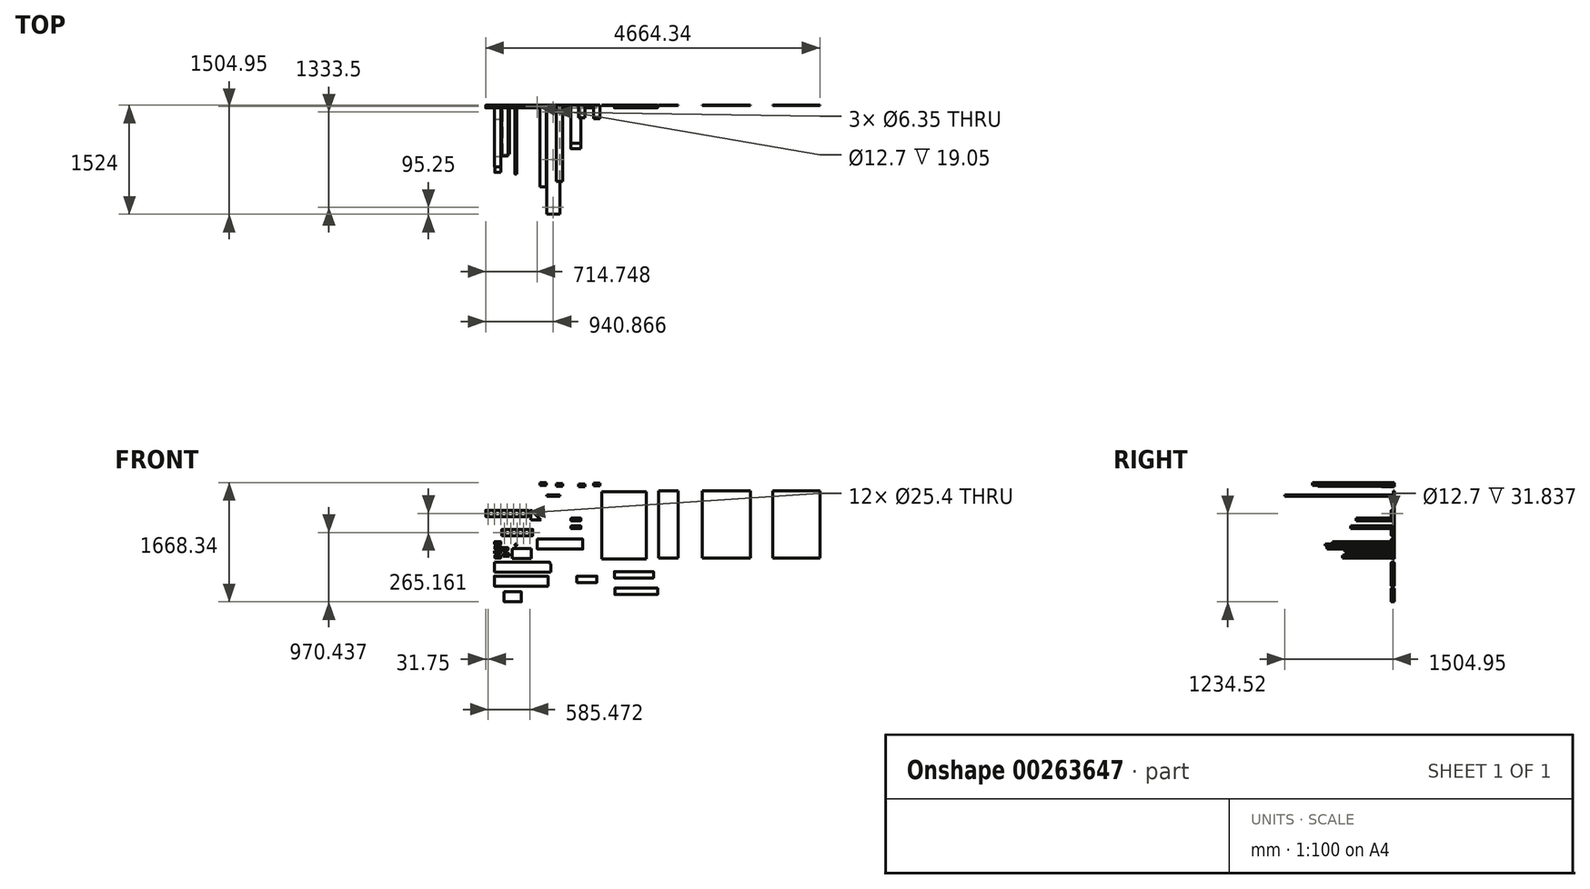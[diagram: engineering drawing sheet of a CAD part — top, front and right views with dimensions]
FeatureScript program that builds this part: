
annotation { "Feature Type Name" : "Feature", "Feature Type Description" : "" }
export const myFeature = defineFeature(function(context is Context, id is Id, definition is map)
    precondition{}
    {
        {
            var Q0;
            Q0=qCreatedBy(makeId("Front.planeOp"),FACE);
            var sketch = newSketch(context, id + "F0", { "sketchPlane" : qUnion([Q0])});
            skLineSegment(sketch, "E0.bottom", {"start": v(-85.66, 61.4) * mm, "end": v(3.24, 61.4) * mm});
            skLineSegment(sketch, "E0.top", {"start": v(-85.66, 23.3) * mm, "end": v(3.24, 23.3) * mm});
            skLineSegment(sketch, "E0.left", {"start": v(-85.66, 61.4) * mm, "end": v(-85.66, 23.3) * mm});
            skLineSegment(sketch, "E0.right", {"start": v(3.24, 61.4) * mm, "end": v(3.24, 23.3) * mm});
            skLineSegment(sketch, "E1.bottom", {"start": v(-85.72, -3.77) * mm, "end": v(3.18, -3.77) * mm});
            skLineSegment(sketch, "E1.top", {"start": v(-85.72, -41.87) * mm, "end": v(3.18, -41.87) * mm});
            skLineSegment(sketch, "E1.left", {"start": v(-85.72, -3.77) * mm, "end": v(-85.72, -41.87) * mm});
            skLineSegment(sketch, "E1.right", {"start": v(3.18, -3.77) * mm, "end": v(3.18, -41.87) * mm});
            skLineSegment(sketch, "E2.bottom", {"start": v(1.48, 88.2) * mm, "end": v(-87.42, 88.2) * mm});
            skLineSegment(sketch, "E2.top", {"start": v(1.48, 126.3) * mm, "end": v(-87.42, 126.3) * mm});
            skLineSegment(sketch, "E2.left", {"start": v(1.48, 88.2) * mm, "end": v(1.48, 126.3) * mm});
            skLineSegment(sketch, "E2.right", {"start": v(-87.42, 88.2) * mm, "end": v(-87.42, 126.3) * mm});
            skLineSegment(sketch, "E3.bottom", {"start": v(3.31, -67.16) * mm, "end": v(-85.59, -67.16) * mm});
            skLineSegment(sketch, "E3.top", {"start": v(3.31, -105.26) * mm, "end": v(-85.59, -105.26) * mm});
            skLineSegment(sketch, "E3.left", {"start": v(3.31, -67.16) * mm, "end": v(3.31, -105.26) * mm});
            skLineSegment(sketch, "E3.right", {"start": v(-85.59, -67.16) * mm, "end": v(-85.59, -105.26) * mm});
            skLineSegment(sketch, "E4.bottom", {"start": v(11.64, 44.1) * mm, "end": v(100.54, 44.1) * mm});
            skLineSegment(sketch, "E4.top", {"start": v(11.64, 6) * mm, "end": v(100.54, 6) * mm});
            skLineSegment(sketch, "E4.left", {"start": v(11.64, 44.1) * mm, "end": v(11.64, 6) * mm});
            skLineSegment(sketch, "E4.right", {"start": v(100.54, 44.1) * mm, "end": v(100.54, 6) * mm});
            skLineSegment(sketch, "E5.bottom", {"start": v(-86.6, -302.76) * mm, "end": v(700.8, -302.76) * mm});
            skLineSegment(sketch, "E5.top", {"start": v(-86.6, -163.06) * mm, "end": v(700.8, -163.06) * mm});
            skLineSegment(sketch, "E5.left", {"start": v(-86.6, -302.76) * mm, "end": v(-86.6, -163.06) * mm});
            skLineSegment(sketch, "E5.right", {"start": v(700.8, -302.76) * mm, "end": v(700.8, -163.06) * mm});
            skLineSegment(sketch, "E6.bottom", {"start": v(425.94, -111) * mm, "end": v(159.24, -111) * mm});
            skLineSegment(sketch, "E6.top", {"start": v(425.94, 28.7) * mm, "end": v(159.24, 28.7) * mm});
            skLineSegment(sketch, "E6.left", {"start": v(425.94, -111) * mm, "end": v(425.94, 28.7) * mm});
            skLineSegment(sketch, "E6.right", {"start": v(159.24, -111) * mm, "end": v(159.24, 28.7) * mm});
            skLineSegment(sketch, "E7.bottom", {"start": v(31.64, -41.5) * mm, "end": v(120.54, -41.5) * mm});
            skLineSegment(sketch, "E7.top", {"start": v(31.64, -79.6) * mm, "end": v(120.54, -79.6) * mm});
            skLineSegment(sketch, "E7.left", {"start": v(31.64, -41.5) * mm, "end": v(31.64, -79.6) * mm});
            skLineSegment(sketch, "E7.right", {"start": v(120.54, -41.5) * mm, "end": v(120.54, -79.6) * mm});
            skLineSegment(sketch, "E8.bottom", {"start": v(178.07, 132.2) * mm, "end": v(266.97, 132.2) * mm});
            skLineSegment(sketch, "E8.top", {"start": v(178.07, 94.1) * mm, "end": v(266.97, 94.1) * mm});
            skLineSegment(sketch, "E8.left", {"start": v(178.07, 132.2) * mm, "end": v(178.07, 94.1) * mm});
            skLineSegment(sketch, "E8.right", {"start": v(266.97, 132.2) * mm, "end": v(266.97, 94.1) * mm});
            skCircle(sketch, "E9", {"center": v(210, 76.86) * mm, "radius": 12.7 * mm});
            skLineSegment(sketch, "E10.bottom", {"start": v(13.97, 297.46) * mm, "end": v(445.77, 297.46) * mm});
            skLineSegment(sketch, "E10.top", {"start": v(13.97, 208.56) * mm, "end": v(445.77, 208.56) * mm});
            skLineSegment(sketch, "E10.left", {"start": v(13.97, 297.46) * mm, "end": v(13.97, 208.56) * mm});
            skLineSegment(sketch, "E10.right", {"start": v(445.77, 297.46) * mm, "end": v(445.77, 208.56) * mm});
            skLineSegment(sketch, "E11", {"start": v(13.97, 253) * mm, "end": v(52.07, 253) * mm});
            skLineSegment(sketch, "E12", {"start": v(52.07, 253) * mm, "end": v(140.97, 253) * mm});
            skLineSegment(sketch, "E13", {"start": v(140.97, 253) * mm, "end": v(229.87, 253) * mm});
            skLineSegment(sketch, "E14", {"start": v(229.87, 253) * mm, "end": v(318.77, 253) * mm});
            skCircle(sketch, "E15", {"center": v(52.07, 253) * mm, "radius": 12.7 * mm});
            skCircle(sketch, "E16", {"center": v(140.97, 253) * mm, "radius": 12.7 * mm});
            skCircle(sketch, "E17", {"center": v(229.87, 253) * mm, "radius": 12.7 * mm});
            skCircle(sketch, "E18", {"center": v(318.77, 253) * mm, "radius": 12.7 * mm});
            skLineSegment(sketch, "E19.bottom", {"start": v(-292.5, 427.6) * mm, "end": v(367.9, 427.6) * mm});
            skLineSegment(sketch, "E19.top", {"start": v(-292.5, 338.7) * mm, "end": v(367.9, 338.7) * mm});
            skLineSegment(sketch, "E19.left", {"start": v(-292.5, 427.6) * mm, "end": v(-292.5, 338.7) * mm});
            skLineSegment(sketch, "E19.right", {"start": v(367.9, 427.6) * mm, "end": v(367.9, 338.7) * mm});
            skLineSegment(sketch, "E20.bottom", {"start": v(-209.55, 562.62) * mm, "end": v(387.35, 562.62) * mm});
            skLineSegment(sketch, "E20.top", {"start": v(-209.55, 473.72) * mm, "end": v(387.35, 473.72) * mm});
            skLineSegment(sketch, "E20.left", {"start": v(-209.55, 562.62) * mm, "end": v(-209.55, 473.72) * mm});
            skLineSegment(sketch, "E20.right", {"start": v(387.35, 562.62) * mm, "end": v(387.35, 473.72) * mm});
            skLineSegment(sketch, "E21", {"start": v(-292.5, 383.15) * mm, "end": v(-254.4, 383.15) * mm});
            skLineSegment(sketch, "E22", {"start": v(-254.4, 383.15) * mm, "end": v(-152.8, 383.15) * mm});
            skLineSegment(sketch, "E23", {"start": v(-152.8, 383.15) * mm, "end": v(-51.2, 383.15) * mm});
            skLineSegment(sketch, "E24", {"start": v(-51.2, 383.15) * mm, "end": v(50.4, 383.15) * mm});
            skLineSegment(sketch, "E25", {"start": v(50.4, 383.15) * mm, "end": v(152, 383.15) * mm});
            skLineSegment(sketch, "E26", {"start": v(152, 383.15) * mm, "end": v(253.6, 383.15) * mm});
            skLineSegment(sketch, "E27", {"start": v(-209.55, 518.17) * mm, "end": v(-177.8, 518.17) * mm});
            skLineSegment(sketch, "E28", {"start": v(-177.8, 518.17) * mm, "end": v(-88.9, 518.17) * mm});
            skLineSegment(sketch, "E29", {"start": v(-88.9, 518.17) * mm, "end": v(0, 518.17) * mm});
            skLineSegment(sketch, "E30", {"start": v(0, 518.17) * mm, "end": v(88.9, 518.17) * mm});
            skLineSegment(sketch, "E31", {"start": v(88.9, 518.17) * mm, "end": v(177.8, 518.17) * mm});
            skLineSegment(sketch, "E32", {"start": v(177.8, 518.17) * mm, "end": v(266.7, 518.17) * mm});
            skCircle(sketch, "E33", {"center": v(-177.8, 518.17) * mm, "radius": 12.7 * mm});
            skCircle(sketch, "E34", {"center": v(-88.9, 518.17) * mm, "radius": 12.7 * mm});
            skCircle(sketch, "E35", {"center": v(0, 518.17) * mm, "radius": 12.7 * mm});
            skCircle(sketch, "E36", {"center": v(88.9, 518.17) * mm, "radius": 12.7 * mm});
            skCircle(sketch, "E37", {"center": v(177.8, 518.17) * mm, "radius": 12.7 * mm});
            skCircle(sketch, "E38", {"center": v(266.7, 518.17) * mm, "radius": 12.7 * mm});
            skCircle(sketch, "E39", {"center": v(-254.4, 383.15) * mm, "radius": 12.7 * mm});
            skCircle(sketch, "E40", {"center": v(-152.8, 383.15) * mm, "radius": 12.7 * mm});
            skCircle(sketch, "E41", {"center": v(-51.2, 383.15) * mm, "radius": 12.7 * mm});
            skCircle(sketch, "E42", {"center": v(50.4, 383.15) * mm, "radius": 12.7 * mm});
            skCircle(sketch, "E43", {"center": v(152, 383.15) * mm, "radius": 12.7 * mm});
            skCircle(sketch, "E44", {"center": v(253.6, 383.15) * mm, "radius": 12.7 * mm});
            skLineSegment(sketch, "E45.bottom", {"start": v(700.8, -163.06) * mm, "end": v(688.1, -163.06) * mm});
            skLineSegment(sketch, "E45.top", {"start": v(700.8, -188.46) * mm, "end": v(688.1, -188.46) * mm});
            skLineSegment(sketch, "E45.left", {"start": v(700.8, -163.06) * mm, "end": v(700.8, -188.46) * mm});
            skLineSegment(sketch, "E45.right", {"start": v(688.1, -163.06) * mm, "end": v(688.1, -188.46) * mm});
            skLineSegment(sketch, "E46.bottom", {"start": v(-89.61, -357.84) * mm, "end": v(659.69, -357.84) * mm});
            skLineSegment(sketch, "E46.top", {"start": v(-89.61, -497.54) * mm, "end": v(659.69, -497.54) * mm});
            skLineSegment(sketch, "E46.left", {"start": v(-89.61, -357.84) * mm, "end": v(-89.61, -497.54) * mm});
            skLineSegment(sketch, "E46.right", {"start": v(659.69, -357.84) * mm, "end": v(659.69, -497.54) * mm});
            skLineSegment(sketch, "E47.bottom", {"start": v(1407.38, 824.95) * mm, "end": v(2029.68, 824.95) * mm});
            skLineSegment(sketch, "E47.top", {"start": v(1407.38, -114.85) * mm, "end": v(2029.68, -114.85) * mm});
            skLineSegment(sketch, "E47.left", {"start": v(1407.38, 824.95) * mm, "end": v(1407.38, -114.85) * mm});
            skLineSegment(sketch, "E47.right", {"start": v(2029.68, 824.95) * mm, "end": v(2029.68, -114.85) * mm});
            skLineSegment(sketch, "E48.bottom", {"start": v(2204.45, 833.86) * mm, "end": v(2477.5, 833.86) * mm});
            skLineSegment(sketch, "E48.top", {"start": v(2204.45, -105.94) * mm, "end": v(2477.5, -105.94) * mm});
            skLineSegment(sketch, "E48.left", {"start": v(2204.45, 833.86) * mm, "end": v(2204.45, -105.94) * mm});
            skLineSegment(sketch, "E48.right", {"start": v(2477.5, 833.86) * mm, "end": v(2477.5, -105.94) * mm});
            skLineSegment(sketch, "E49.bottom", {"start": v(2811.62, 833.86) * mm, "end": v(3484.72, 833.86) * mm});
            skLineSegment(sketch, "E49.top", {"start": v(2811.62, -105.94) * mm, "end": v(3484.72, -105.94) * mm});
            skLineSegment(sketch, "E49.left", {"start": v(2811.62, 833.86) * mm, "end": v(2811.62, -105.94) * mm});
            skLineSegment(sketch, "E49.right", {"start": v(3484.72, 833.86) * mm, "end": v(3484.72, -105.94) * mm});
            skLineSegment(sketch, "E50", {"start": v(266.7, 518.17) * mm, "end": v(355.6, 518.17) * mm});
            skCircle(sketch, "E51", {"center": v(355.6, 518.17) * mm, "radius": 12.7 * mm});
            skLineSegment(sketch, "E52", {"start": v(318.77, 253) * mm, "end": v(407.67, 253) * mm});
            skCircle(sketch, "E53", {"center": v(407.67, 253) * mm, "radius": 12.7 * mm});
            skLineSegment(sketch, "E54.bottom", {"start": v(416.3, 567.9) * mm, "end": v(556, 567.9) * mm});
            skLineSegment(sketch, "E54.top", {"start": v(416.3, 428.2) * mm, "end": v(556, 428.2) * mm});
            skLineSegment(sketch, "E54.left", {"start": v(416.3, 567.9) * mm, "end": v(416.3, 428.2) * mm});
            skLineSegment(sketch, "E54.right", {"start": v(556, 567.9) * mm, "end": v(556, 428.2) * mm});
            skLineSegment(sketch, "E55", {"start": v(416.3, 567.9) * mm, "end": v(556, 428.2) * mm});
            skLineSegment(sketch, "E56.bottom", {"start": v(980.9, 453.14) * mm, "end": v(1120.6, 453.14) * mm});
            skLineSegment(sketch, "E56.top", {"start": v(980.9, 415.04) * mm, "end": v(1120.6, 415.04) * mm});
            skLineSegment(sketch, "E56.left", {"start": v(980.9, 453.14) * mm, "end": v(980.9, 415.04) * mm});
            skLineSegment(sketch, "E56.right", {"start": v(1120.6, 453.14) * mm, "end": v(1120.6, 415.04) * mm});
            skLineSegment(sketch, "E57.bottom", {"start": v(980.9, 343.92) * mm, "end": v(1120.6, 343.92) * mm});
            skLineSegment(sketch, "E57.top", {"start": v(980.9, 305.82) * mm, "end": v(1120.6, 305.82) * mm});
            skLineSegment(sketch, "E57.left", {"start": v(980.9, 343.92) * mm, "end": v(980.9, 305.82) * mm});
            skLineSegment(sketch, "E57.right", {"start": v(1120.6, 343.92) * mm, "end": v(1120.6, 305.82) * mm});
            skLineSegment(sketch, "E58.bottom", {"start": v(509.36, 160.8) * mm, "end": v(1144.36, 160.8) * mm});
            skLineSegment(sketch, "E58.top", {"start": v(509.36, 21.1) * mm, "end": v(1144.36, 21.1) * mm});
            skLineSegment(sketch, "E58.left", {"start": v(509.36, 160.8) * mm, "end": v(509.36, 21.1) * mm});
            skLineSegment(sketch, "E58.right", {"start": v(1144.36, 160.8) * mm, "end": v(1144.36, 21.1) * mm});
            skLineSegment(sketch, "E59.bottom", {"start": v(2132.43, -293.4) * mm, "end": v(1586.33, -293.4) * mm});
            skLineSegment(sketch, "E59.top", {"start": v(2132.43, -382.3) * mm, "end": v(1586.33, -382.3) * mm});
            skLineSegment(sketch, "E59.left", {"start": v(2132.43, -293.4) * mm, "end": v(2132.43, -382.3) * mm});
            skLineSegment(sketch, "E59.right", {"start": v(1586.33, -293.4) * mm, "end": v(1586.33, -382.3) * mm});
            skLineSegment(sketch, "E60.bottom", {"start": v(2190.62, -526.52) * mm, "end": v(1593.72, -526.52) * mm});
            skLineSegment(sketch, "E60.top", {"start": v(2190.62, -615.42) * mm, "end": v(1593.72, -615.42) * mm});
            skLineSegment(sketch, "E60.left", {"start": v(2190.62, -526.52) * mm, "end": v(2190.62, -615.42) * mm});
            skLineSegment(sketch, "E60.right", {"start": v(1593.72, -526.52) * mm, "end": v(1593.72, -615.42) * mm});
            skLineSegment(sketch, "E61.bottom", {"start": v(1062.38, -357.34) * mm, "end": v(1341.78, -357.34) * mm});
            skLineSegment(sketch, "E61.top", {"start": v(1062.38, -446.24) * mm, "end": v(1341.78, -446.24) * mm});
            skLineSegment(sketch, "E61.left", {"start": v(1062.38, -357.34) * mm, "end": v(1062.38, -446.24) * mm});
            skLineSegment(sketch, "E61.right", {"start": v(1341.78, -357.34) * mm, "end": v(1341.78, -446.24) * mm});
            skLineSegment(sketch, "E62.bottom", {"start": v(47.05, -577.73) * mm, "end": v(288.35, -577.73) * mm});
            skLineSegment(sketch, "E62.top", {"start": v(47.05, -717.43) * mm, "end": v(288.35, -717.43) * mm});
            skLineSegment(sketch, "E62.left", {"start": v(47.05, -577.73) * mm, "end": v(47.05, -717.43) * mm});
            skLineSegment(sketch, "E62.right", {"start": v(288.35, -577.73) * mm, "end": v(288.35, -717.43) * mm});
            skLineSegment(sketch, "E63.bottom", {"start": v(3794.39, 833.86) * mm, "end": v(4454.79, 833.86) * mm});
            skLineSegment(sketch, "E63.top", {"start": v(3794.39, -105.94) * mm, "end": v(4454.79, -105.94) * mm});
            skLineSegment(sketch, "E63.left", {"start": v(3794.39, 833.86) * mm, "end": v(3794.39, -105.94) * mm});
            skLineSegment(sketch, "E63.right", {"start": v(4454.79, 833.86) * mm, "end": v(4454.79, -105.94) * mm});
            skLineSegment(sketch, "E64.bottom", {"start": v(549.17, 950.91) * mm, "end": v(638.07, 950.91) * mm});
            skLineSegment(sketch, "E64.top", {"start": v(549.17, 912.81) * mm, "end": v(638.07, 912.81) * mm});
            skLineSegment(sketch, "E64.left", {"start": v(549.17, 950.91) * mm, "end": v(549.17, 912.81) * mm});
            skLineSegment(sketch, "E64.right", {"start": v(638.07, 950.91) * mm, "end": v(638.07, 912.81) * mm});
            skLineSegment(sketch, "E65.bottom", {"start": v(774.22, 935.7) * mm, "end": v(863.12, 935.7) * mm});
            skLineSegment(sketch, "E65.top", {"start": v(774.22, 897.6) * mm, "end": v(863.12, 897.6) * mm});
            skLineSegment(sketch, "E65.left", {"start": v(774.22, 935.7) * mm, "end": v(774.22, 897.6) * mm});
            skLineSegment(sketch, "E65.right", {"start": v(863.12, 935.7) * mm, "end": v(863.12, 897.6) * mm});
            skLineSegment(sketch, "E66.bottom", {"start": v(1087.47, 929.62) * mm, "end": v(1176.37, 929.62) * mm});
            skLineSegment(sketch, "E66.top", {"start": v(1087.47, 891.52) * mm, "end": v(1176.37, 891.52) * mm});
            skLineSegment(sketch, "E66.left", {"start": v(1087.47, 929.62) * mm, "end": v(1087.47, 891.52) * mm});
            skLineSegment(sketch, "E66.right", {"start": v(1176.37, 929.62) * mm, "end": v(1176.37, 891.52) * mm});
            skLineSegment(sketch, "E67.bottom", {"start": v(1293.65, 941.37) * mm, "end": v(1382.55, 941.37) * mm});
            skLineSegment(sketch, "E67.top", {"start": v(1293.65, 903.27) * mm, "end": v(1382.55, 903.27) * mm});
            skLineSegment(sketch, "E67.left", {"start": v(1293.65, 941.37) * mm, "end": v(1293.65, 903.27) * mm});
            skLineSegment(sketch, "E67.right", {"start": v(1382.55, 941.37) * mm, "end": v(1382.55, 903.27) * mm});
            skLineSegment(sketch, "E68.bottom", {"start": v(642.42, 775.35) * mm, "end": v(826.57, 775.35) * mm});
            skLineSegment(sketch, "E68.top", {"start": v(642.42, 756.3) * mm, "end": v(826.57, 756.3) * mm});
            skLineSegment(sketch, "E68.left", {"start": v(642.42, 775.35) * mm, "end": v(642.42, 756.3) * mm});
            skLineSegment(sketch, "E68.right", {"start": v(826.57, 775.35) * mm, "end": v(826.57, 756.3) * mm});
            skSolve(sketch);
        }
        {
            var Q0;
            Q0=makeQuery(id+"F0.imprint","IMPRINT",FACE,{"disambiguationData":[TD([[makeQuery(id+"F0.imprint","IMPRINT",EDGE,{"derivedFrom":sQuery(id+"F0.wireOp",EDGE,"E0.bottom")}),-1.0]])]});
            var Q1;
            {var subQ0=sQuery(id+"F0.wireOp",EDGE,"cPqlnZu6-hQf6-qhiV-5iE7-ykGDKPtnwq6q");var subQ4=makeQuery(id+"F0.imprint","IMPRINT",VERTEX,{"derivedFrom":subQ0});Q1=makeQuery(id+"F0.imprint","IMPRINT",FACE,{"disambiguationData":[TD([[makeQuery(id+"F0.imprint","IMPRINT",EDGE,{"disambiguationData":[TD([[subQ4,1.0]])],"derivedFrom":subQ0}),-1.0]])]});}
            extrude(context, id + "F1", {"entities" : qUnion([Q0, Q1]), "depth" : 939.8 * mm});
        }
        {
            var Q0;
            Q0=makeQuery(id+"F1.opExtrude","SWEPT_EDGE",EDGE,{"disambiguationData":[OSD([sQuery(id+"F0.wireOp",EDGE,"E0.bottom"),sQuery(id+"F0.wireOp",EDGE,"E0.left")])]});
            var Q1;
            Q1=makeQuery(id+"F1.opExtrude","SWEPT_EDGE",EDGE,{"disambiguationData":[OSD([sQuery(id+"F0.wireOp",EDGE,"E0.top"),sQuery(id+"F0.wireOp",EDGE,"E0.left")])]});
            var Q2;
            Q2=makeQuery(id+"F1.opExtrude","SWEPT_EDGE",EDGE,{"disambiguationData":[OSD([sQuery(id+"F0.wireOp",EDGE,"E0.bottom"),sQuery(id+"F0.wireOp",EDGE,"E0.right")])]});
            var Q3;
            Q3=makeQuery(id+"F1.opExtrude","SWEPT_EDGE",EDGE,{"disambiguationData":[OSD([sQuery(id+"F0.wireOp",EDGE,"E0.top"),sQuery(id+"F0.wireOp",EDGE,"E0.right")])]});
            fillet(context, id + "F2", {"entities" : qUnion([Q0, Q1, Q2, Q3]), "radius" : 5.08 * mm, "tangentPropagation" : true, "allowEdgeOverflow" : false});
        }
        {
            var Q0;
            Q0=makeQuery(id+"F0.imprint","IMPRINT",FACE,{"disambiguationData":[TD([[makeQuery(id+"F0.imprint","IMPRINT",EDGE,{"derivedFrom":sQuery(id+"F0.wireOp",EDGE,"E2.bottom")}),-1.0]])]});
            extrude(context, id + "F3", {"entities" : qUnion([Q0]), "depth" : 863.6 * mm});
        }
        {
            var Q0;
            Q0=makeQuery(id+"F0.imprint","IMPRINT",FACE,{"disambiguationData":[TD([[makeQuery(id+"F0.imprint","IMPRINT",EDGE,{"derivedFrom":sQuery(id+"F0.wireOp",EDGE,"E4.bottom")}),-1.0]])]});
            extrude(context, id + "F4", {"entities" : qUnion([Q0]), "depth" : 711.2 * mm});
        }
        {
            var Q0;
            Q0=makeQuery(id+"F0.imprint","IMPRINT",FACE,{"disambiguationData":[TD([[makeQuery(id+"F0.imprint","IMPRINT",EDGE,{"derivedFrom":sQuery(id+"F0.wireOp",EDGE,"E6.bottom")}),-1.0]])]});
            extrude(context, id + "F5", {"entities" : qUnion([Q0]), "depth" : 38.1 * mm});
        }
        {
            var Q0;
            Q0=makeQuery(id+"F0.imprint","IMPRINT",FACE,{"disambiguationData":[TD([[makeQuery(id+"F0.imprint","IMPRINT",EDGE,{"derivedFrom":sQuery(id+"F0.wireOp",EDGE,"E5.bottom")}),1.0]])]});
            extrude(context, id + "F6", {"entities" : qUnion([Q0]), "depth" : 38.1 * mm});
        }
        {
            var Q0;
            Q0=makeQuery(id+"F3.opExtrude","SWEPT_EDGE",EDGE,{"disambiguationData":[OSD([sQuery(id+"F0.wireOp",EDGE,"E2.top"),sQuery(id+"F0.wireOp",EDGE,"E2.left")])]});
            var Q1;
            Q1=makeQuery(id+"F3.opExtrude","SWEPT_EDGE",EDGE,{"disambiguationData":[OSD([sQuery(id+"F0.wireOp",EDGE,"E2.bottom"),sQuery(id+"F0.wireOp",EDGE,"E2.left")])]});
            var Q2;
            Q2=makeQuery(id+"F4.opExtrude","SWEPT_EDGE",EDGE,{"disambiguationData":[OSD([sQuery(id+"F0.wireOp",EDGE,"E4.bottom"),sQuery(id+"F0.wireOp",EDGE,"E4.right")])]});
            var Q3;
            Q3=makeQuery(id+"F4.opExtrude","SWEPT_EDGE",EDGE,{"disambiguationData":[OSD([sQuery(id+"F0.wireOp",EDGE,"E4.top"),sQuery(id+"F0.wireOp",EDGE,"E4.right")])]});
            var Q4;
            Q4=makeQuery(id+"F6.opExtrude","CAP_EDGE",EDGE,{"disambiguationData":[OSD([sQuery(id+"F0.wireOp",EDGE,"E5.top")])],"isStart":false});
            var Q5;
            Q5=makeQuery(id+"F6.opExtrude","CAP_EDGE",EDGE,{"disambiguationData":[OSD([sQuery(id+"F0.wireOp",EDGE,"E5.top")])],"isStart":true});
            var Q6;
            Q6=makeQuery(id+"F5.opExtrude","CAP_EDGE",EDGE,{"disambiguationData":[OSD([sQuery(id+"F0.wireOp",EDGE,"E6.top")])],"isStart":false});
            var Q7;
            Q7=makeQuery(id+"F5.opExtrude","CAP_EDGE",EDGE,{"disambiguationData":[OSD([sQuery(id+"F0.wireOp",EDGE,"E6.top")])],"isStart":true});
            var Q8;
            Q8=makeQuery(id+"F4.opExtrude","SWEPT_EDGE",EDGE,{"disambiguationData":[OSD([sQuery(id+"F0.wireOp",EDGE,"E4.top"),sQuery(id+"F0.wireOp",EDGE,"E4.left")])]});
            var Q9;
            Q9=makeQuery(id+"F4.opExtrude","SWEPT_EDGE",EDGE,{"disambiguationData":[OSD([sQuery(id+"F0.wireOp",EDGE,"E4.bottom"),sQuery(id+"F0.wireOp",EDGE,"E4.left")])]});
            var Q10;
            Q10=makeQuery(id+"F3.opExtrude","SWEPT_EDGE",EDGE,{"disambiguationData":[OSD([sQuery(id+"F0.wireOp",EDGE,"E2.bottom"),sQuery(id+"F0.wireOp",EDGE,"E2.right")])]});
            var Q11;
            Q11=makeQuery(id+"F3.opExtrude","SWEPT_EDGE",EDGE,{"disambiguationData":[OSD([sQuery(id+"F0.wireOp",EDGE,"E2.top"),sQuery(id+"F0.wireOp",EDGE,"E2.right")])]});
            var Q12;
            Q12=makeQuery(id+"F6.opExtrude","CAP_EDGE",EDGE,{"disambiguationData":[OSD([sQuery(id+"F0.wireOp",EDGE,"E5.bottom")])],"isStart":false});
            var Q13;
            Q13=makeQuery(id+"F6.opExtrude","CAP_EDGE",EDGE,{"disambiguationData":[OSD([sQuery(id+"F0.wireOp",EDGE,"E5.bottom")])],"isStart":true});
            var Q14;
            Q14=makeQuery(id+"F5.opExtrude","CAP_EDGE",EDGE,{"disambiguationData":[OSD([sQuery(id+"F0.wireOp",EDGE,"E6.bottom")])],"isStart":false});
            var Q15;
            Q15=makeQuery(id+"F5.opExtrude","CAP_EDGE",EDGE,{"disambiguationData":[OSD([sQuery(id+"F0.wireOp",EDGE,"E6.bottom")])],"isStart":true});
            fillet(context, id + "F7", {"entities" : qUnion([Q0, Q1, Q2, Q3, Q4, Q5, Q6, Q7, Q8, Q9, Q10, Q11, Q12, Q13, Q14, Q15]), "radius" : 5.08 * mm, "tangentPropagation" : true, "allowEdgeOverflow" : false});
        }
        {
            var Q0;
            Q0=makeQuery(id+"F0.imprint","IMPRINT",FACE,{"disambiguationData":[TD([[makeQuery(id+"F0.imprint","IMPRINT",EDGE,{"derivedFrom":sQuery(id+"F0.wireOp",EDGE,"E3.bottom")}),1.0]])]});
            extrude(context, id + "F8", {"entities" : qUnion([Q0]), "depth" : 723.9 * mm});
        }
        {
            var Q0;
            Q0=makeQuery(id+"F8.opExtrude","SWEPT_EDGE",EDGE,{"disambiguationData":[OSD([sQuery(id+"F0.wireOp",EDGE,"E3.bottom"),sQuery(id+"F0.wireOp",EDGE,"E3.left")])]});
            var Q1;
            Q1=makeQuery(id+"F8.opExtrude","SWEPT_EDGE",EDGE,{"disambiguationData":[OSD([sQuery(id+"F0.wireOp",EDGE,"E3.bottom"),sQuery(id+"F0.wireOp",EDGE,"E3.right")])]});
            var Q2;
            Q2=makeQuery(id+"F8.opExtrude","SWEPT_EDGE",EDGE,{"disambiguationData":[OSD([sQuery(id+"F0.wireOp",EDGE,"E3.top"),sQuery(id+"F0.wireOp",EDGE,"E3.left")])]});
            var Q3;
            Q3=makeQuery(id+"F8.opExtrude","SWEPT_EDGE",EDGE,{"disambiguationData":[OSD([sQuery(id+"F0.wireOp",EDGE,"E3.top"),sQuery(id+"F0.wireOp",EDGE,"E3.right")])]});
            fillet(context, id + "F9", {"entities" : qUnion([Q0, Q1, Q2, Q3]), "radius" : 5.08 * mm, "tangentPropagation" : true, "allowEdgeOverflow" : false});
        }
        {
            var Q0;
            Q0=makeQuery(id+"F0.imprint","IMPRINT",FACE,{"disambiguationData":[TD([[makeQuery(id+"F0.imprint","IMPRINT",EDGE,{"derivedFrom":sQuery(id+"F0.wireOp",EDGE,"E1.bottom")}),-1.0]])]});
            extrude(context, id + "F10", {"entities" : qUnion([Q0]), "depth" : 196.85 * mm});
        }
        {
            var Q0;
            Q0=makeQuery(id+"F0.imprint","IMPRINT",FACE,{"disambiguationData":[TD([[makeQuery(id+"F0.imprint","IMPRINT",EDGE,{"derivedFrom":sQuery(id+"F0.wireOp",EDGE,"E7.bottom")}),-1.0]])]});
            extrude(context, id + "F11", {"entities" : qUnion([Q0]), "depth" : 685.8 * mm});
        }
        {
            var Q0;
            Q0=makeQuery(id+"F0.imprint","IMPRINT",FACE,{"disambiguationData":[TD([[makeQuery(id+"F0.imprint","IMPRINT",EDGE,{"derivedFrom":sQuery(id+"F0.wireOp",EDGE,"E8.bottom")}),-1.0]])]});
            extrude(context, id + "F12", {"entities" : qUnion([Q0]), "depth" : 571.5 * mm});
        }
        {
            var Q0;
            Q0=makeQuery(id+"F0.imprint","IMPRINT",FACE,{"disambiguationData":[TD([[makeQuery(id+"F0.imprint","IMPRINT",EDGE,{"derivedFrom":sQuery(id+"F0.wireOp",EDGE,"E9")}),1.0]])]});
            extrude(context, id + "F13", {"entities" : qUnion([Q0]), "depth" : 965.2 * mm});
        }
        {
            var Q0;
            {var subQ12=sQuery(id+"F0.wireOp",EDGE,"E10.bottom");Q0=makeQuery(id+"F0.imprint","IMPRINT",FACE,{"disambiguationData":[TD([[makeQuery(id+"F0.imprint","IMPRINT",EDGE,{"derivedFrom":subQ12}),-1.0]])]});}
            extrude(context, id + "F14", {"entities" : qUnion([Q0]), "depth" : 38.1 * mm});
        }
        {
            var Q0;
            Q0=makeQuery(id+"F12.opExtrude","SWEPT_BODY",BODY,{"disambiguationData":[OSD([sQuery(id+"F0.wireOp",EDGE,"E8.bottom"),sQuery(id+"F0.wireOp",EDGE,"E8.top"),sQuery(id+"F0.wireOp",EDGE,"E8.left"),sQuery(id+"F0.wireOp",EDGE,"E8.right")])]});
            deleteBodies(context, id + "F15", {"entities" : qUnion([Q0])});
        }
        {
            var Q0;
            {var subQ15=sQuery(id+"F0.wireOp",EDGE,"E20.bottom");Q0=makeQuery(id+"F0.imprint","IMPRINT",FACE,{"disambiguationData":[TD([[makeQuery(id+"F0.imprint","IMPRINT",EDGE,{"derivedFrom":subQ15}),-1.0]])]});}
            extrude(context, id + "F16", {"entities" : qUnion([Q0]), "depth" : 38.1 * mm});
        }
        {
            var Q0;
            Q0=makeQuery(id+"F16.opExtrude","CAP_EDGE",EDGE,{"disambiguationData":[OSD([sQuery(id+"F0.wireOp",EDGE,"E20.bottom")])],"isStart":false});
            var Q1;
            Q1=makeQuery(id+"F16.opExtrude","CAP_EDGE",EDGE,{"disambiguationData":[OSD([sQuery(id+"F0.wireOp",EDGE,"E20.top")])],"isStart":false});
            var Q2;
            Q2=makeQuery(id+"F16.opExtrude","CAP_EDGE",EDGE,{"disambiguationData":[OSD([sQuery(id+"F0.wireOp",EDGE,"E20.top")])],"isStart":true});
            var Q3;
            Q3=makeQuery(id+"F14.opExtrude","CAP_EDGE",EDGE,{"disambiguationData":[OSD([sQuery(id+"F0.wireOp",EDGE,"E10.bottom")])],"isStart":false});
            var Q4;
            Q4=makeQuery(id+"F14.opExtrude","CAP_EDGE",EDGE,{"disambiguationData":[OSD([sQuery(id+"F0.wireOp",EDGE,"E10.top")])],"isStart":false});
            var Q5;
            Q5=makeQuery(id+"F14.opExtrude","CAP_EDGE",EDGE,{"disambiguationData":[OSD([sQuery(id+"F0.wireOp",EDGE,"E10.top")])],"isStart":true});
            var Q6;
            Q6=makeQuery(id+"F14.opExtrude","CAP_EDGE",EDGE,{"disambiguationData":[OSD([sQuery(id+"F0.wireOp",EDGE,"E10.bottom")])],"isStart":true});
            var Q7;
            Q7=makeQuery(id+"F16.opExtrude","CAP_EDGE",EDGE,{"disambiguationData":[OSD([sQuery(id+"F0.wireOp",EDGE,"E20.bottom")])],"isStart":true});
            fillet(context, id + "F17", {"entities" : qUnion([Q0, Q1, Q2, Q3, Q4, Q5, Q6, Q7]), "radius" : 5.08 * mm, "tangentPropagation" : true, "allowEdgeOverflow" : false});
        }
        {
            var Q0;
            Q0=makeQuery(id+"F0.imprint","IMPRINT",FACE,{"disambiguationData":[TD([[makeQuery(id+"F0.imprint","IMPRINT",EDGE,{"derivedFrom":sQuery(id+"F0.wireOp",EDGE,"E46.bottom")}),-1.0]])]});
            extrude(context, id + "F18", {"entities" : qUnion([Q0]), "depth" : 38.1 * mm});
        }
        {
            var Q0;
            Q0=makeQuery(id+"F18.opExtrude","CAP_EDGE",EDGE,{"disambiguationData":[OSD([sQuery(id+"F0.wireOp",EDGE,"E46.bottom")])],"isStart":false});
            var Q1;
            Q1=makeQuery(id+"F18.opExtrude","CAP_EDGE",EDGE,{"disambiguationData":[OSD([sQuery(id+"F0.wireOp",EDGE,"E46.top")])],"isStart":false});
            var Q2;
            Q2=makeQuery(id+"F18.opExtrude","CAP_EDGE",EDGE,{"disambiguationData":[OSD([sQuery(id+"F0.wireOp",EDGE,"E46.bottom")])],"isStart":true});
            var Q3;
            Q3=makeQuery(id+"F18.opExtrude","CAP_EDGE",EDGE,{"disambiguationData":[OSD([sQuery(id+"F0.wireOp",EDGE,"E46.top")])],"isStart":true});
            fillet(context, id + "F19", {"entities" : qUnion([Q0, Q1, Q2, Q3]), "radius" : 5.08 * mm, "tangentPropagation" : true, "allowEdgeOverflow" : false});
        }
        {
            var Q0;
            Q0=makeQuery(id+"F0.imprint","IMPRINT",FACE,{"disambiguationData":[TD([[makeQuery(id+"F0.imprint","IMPRINT",EDGE,{"derivedFrom":sQuery(id+"F0.wireOp",EDGE,"E47.bottom")}),-1.0]])]});
            extrude(context, id + "F20", {"entities" : qUnion([Q0]), "depth" : 6.35 * mm});
        }
        {
            var Q0;
            Q0=makeQuery(id+"F0.imprint","IMPRINT",FACE,{"disambiguationData":[TD([[makeQuery(id+"F0.imprint","IMPRINT",EDGE,{"derivedFrom":sQuery(id+"F0.wireOp",EDGE,"E48.bottom")}),-1.0]])]});
            extrude(context, id + "F21", {"entities" : qUnion([Q0]), "depth" : 6.35 * mm});
        }
        {
            var Q0;
            Q0=makeQuery(id+"F0.imprint","IMPRINT",FACE,{"disambiguationData":[TD([[makeQuery(id+"F0.imprint","IMPRINT",EDGE,{"derivedFrom":sQuery(id+"F0.wireOp",EDGE,"E49.bottom")}),-1.0]])]});
            extrude(context, id + "F22", {"entities" : qUnion([Q0]), "depth" : 6.35 * mm});
        }
        {
            var Q0;
            Q0=makeQuery(id+"F0.imprint","IMPRINT",FACE,{"disambiguationData":[TD([[makeQuery(id+"F0.imprint","IMPRINT",EDGE,{"derivedFrom":sQuery(id+"F0.wireOp",EDGE,"E54.top")}),1.0]])]});
            extrude(context, id + "F23", {"entities" : qUnion([Q0]), "depth" : 38.1 * mm});
        }
        {
            var Q0;
            Q0=makeQuery(id+"F23.opExtrude","CAP_EDGE",EDGE,{"disambiguationData":[OSD([sQuery(id+"F0.wireOp",EDGE,"E55")])],"isStart":false});
            var Q1;
            Q1=makeQuery(id+"F23.opExtrude","CAP_EDGE",EDGE,{"disambiguationData":[OSD([sQuery(id+"F0.wireOp",EDGE,"E55")])],"isStart":true});
            fillet(context, id + "F24", {"entities" : qUnion([Q0, Q1]), "radius" : 5.08 * mm, "tangentPropagation" : true, "allowEdgeOverflow" : false});
        }
        {
            var Q0;
            Q0=makeQuery(id+"F23.opExtrude","SWEPT_FACE",FACE,{"disambiguationData":[OSD([sQuery(id+"F0.wireOp",EDGE,"E54.top")])]});
            var sketch = newSketch(context, id + "F25", { "sketchPlane" : qUnion([Q0])});
            skLineSegment(sketch, "E69", {"start": v(416.3, 19.05) * mm, "end": v(505.2, 19.05) * mm});
            skCircle(sketch, "E70", {"center": v(505.2, 19.05) * mm, "radius": 6.35 * mm});
            skSolve(sketch);
        }
        {
            var Q0;
            Q0=makeQuery(id+"F25.imprint","IMPRINT",FACE,{"disambiguationData":[TD([[makeQuery(id+"F25.imprint","IMPRINT",EDGE,{"derivedFrom":sQuery(id+"F25.wireOp",EDGE,"E70")}),1.0]])]});
            extrude(context, id + "F26", {"entities" : qUnion([Q0]), "operationType" : NewBodyOperationType.REMOVE, "oppositeDirection" : true, "depth" : 76.2 * mm, "hasSecondDirection" : true, "secondDirectionOppositeDirection" : true, "secondDirectionDepth" : 38.1 * mm});
        }
        {
            var Q0;
            Q0=makeQuery(id+"F23.opExtrude","SWEPT_FACE",FACE,{"disambiguationData":[OSD([sQuery(id+"F0.wireOp",EDGE,"E54.left")])]});
            var sketch = newSketch(context, id + "F27", { "sketchPlane" : qUnion([Q0])});
            skLineSegment(sketch, "E71", {"start": v(19.05, 428.2) * mm, "end": v(19.05, 517.1) * mm});
            skCircle(sketch, "E72", {"center": v(19.05, 517.1) * mm, "radius": 6.35 * mm});
            skSolve(sketch);
        }
        {
            var Q0;
            Q0=makeQuery(id+"F27.imprint","IMPRINT",FACE,{"disambiguationData":[TD([[makeQuery(id+"F27.imprint","IMPRINT",EDGE,{"derivedFrom":sQuery(id+"F27.wireOp",EDGE,"E72")}),1.0]])]});
            extrude(context, id + "F28", {"entities" : qUnion([Q0]), "operationType" : NewBodyOperationType.REMOVE, "oppositeDirection" : true, "depth" : 76.2 * mm, "hasSecondDirection" : true, "secondDirectionOppositeDirection" : true, "secondDirectionDepth" : 25.4 * mm});
        }
        {
            var Q0;
            Q0=makeQuery(id+"F0.imprint","IMPRINT",FACE,{"disambiguationData":[TD([[makeQuery(id+"F0.imprint","IMPRINT",EDGE,{"derivedFrom":sQuery(id+"F0.wireOp",EDGE,"E56.bottom")}),-1.0]])]});
            extrude(context, id + "F29", {"entities" : qUnion([Q0]), "depth" : 533.4 * mm});
        }
        {
            var Q0;
            Q0=makeQuery(id+"F0.imprint","IMPRINT",FACE,{"disambiguationData":[TD([[makeQuery(id+"F0.imprint","IMPRINT",EDGE,{"derivedFrom":sQuery(id+"F0.wireOp",EDGE,"E57.bottom")}),-1.0]])]});
            extrude(context, id + "F30", {"entities" : qUnion([Q0]), "depth" : 609.6 * mm});
        }
        {
            var Q0;
            Q0=makeQuery(id+"F29.opExtrude","SWEPT_EDGE",EDGE,{"disambiguationData":[OSD([sQuery(id+"F0.wireOp",EDGE,"E56.bottom"),sQuery(id+"F0.wireOp",EDGE,"E56.left")])]});
            var Q1;
            Q1=makeQuery(id+"F29.opExtrude","SWEPT_EDGE",EDGE,{"disambiguationData":[OSD([sQuery(id+"F0.wireOp",EDGE,"E56.top"),sQuery(id+"F0.wireOp",EDGE,"E56.left")])]});
            var Q2;
            Q2=makeQuery(id+"F29.opExtrude","SWEPT_EDGE",EDGE,{"disambiguationData":[OSD([sQuery(id+"F0.wireOp",EDGE,"E56.top"),sQuery(id+"F0.wireOp",EDGE,"E56.right")])]});
            var Q3;
            Q3=makeQuery(id+"F30.opExtrude","SWEPT_EDGE",EDGE,{"disambiguationData":[OSD([sQuery(id+"F0.wireOp",EDGE,"E57.bottom"),sQuery(id+"F0.wireOp",EDGE,"E57.left")])]});
            var Q4;
            Q4=makeQuery(id+"F30.opExtrude","SWEPT_EDGE",EDGE,{"disambiguationData":[OSD([sQuery(id+"F0.wireOp",EDGE,"E57.top"),sQuery(id+"F0.wireOp",EDGE,"E57.left")])]});
            var Q5;
            Q5=makeQuery(id+"F30.opExtrude","SWEPT_EDGE",EDGE,{"disambiguationData":[OSD([sQuery(id+"F0.wireOp",EDGE,"E57.top"),sQuery(id+"F0.wireOp",EDGE,"E57.right")])]});
            var Q6;
            Q6=makeQuery(id+"F29.opExtrude","SWEPT_EDGE",EDGE,{"disambiguationData":[OSD([sQuery(id+"F0.wireOp",EDGE,"E56.bottom"),sQuery(id+"F0.wireOp",EDGE,"E56.right")])]});
            var Q7;
            Q7=makeQuery(id+"F30.opExtrude","SWEPT_EDGE",EDGE,{"disambiguationData":[OSD([sQuery(id+"F0.wireOp",EDGE,"E57.bottom"),sQuery(id+"F0.wireOp",EDGE,"E57.right")])]});
            fillet(context, id + "F31", {"entities" : qUnion([Q0, Q1, Q2, Q3, Q4, Q5, Q6, Q7]), "radius" : 5.08 * mm, "tangentPropagation" : true, "allowEdgeOverflow" : false});
        }
        {
            var Q0;
            Q0=makeQuery(id+"F0.imprint","IMPRINT",FACE,{"disambiguationData":[TD([[makeQuery(id+"F0.imprint","IMPRINT",EDGE,{"derivedFrom":sQuery(id+"F0.wireOp",EDGE,"E58.bottom")}),-1.0]])]});
            extrude(context, id + "F32", {"entities" : qUnion([Q0]), "depth" : 38.1 * mm});
        }
        {
            var Q0;
            Q0=makeQuery(id+"F32.opExtrude","CAP_EDGE",EDGE,{"disambiguationData":[OSD([sQuery(id+"F0.wireOp",EDGE,"E58.top")])],"isStart":false});
            var Q1;
            Q1=makeQuery(id+"F32.opExtrude","CAP_EDGE",EDGE,{"disambiguationData":[OSD([sQuery(id+"F0.wireOp",EDGE,"E58.bottom")])],"isStart":false});
            var Q2;
            Q2=makeQuery(id+"F32.opExtrude","CAP_EDGE",EDGE,{"disambiguationData":[OSD([sQuery(id+"F0.wireOp",EDGE,"E58.bottom")])],"isStart":true});
            var Q3;
            Q3=makeQuery(id+"F32.opExtrude","CAP_EDGE",EDGE,{"disambiguationData":[OSD([sQuery(id+"F0.wireOp",EDGE,"E58.top")])],"isStart":true});
            fillet(context, id + "F33", {"entities" : qUnion([Q0, Q1, Q2, Q3]), "radius" : 5.08 * mm, "tangentPropagation" : true, "allowEdgeOverflow" : false});
        }
        {
            var Q0;
            Q0=makeQuery(id+"F0.imprint","IMPRINT",FACE,{"disambiguationData":[TD([[makeQuery(id+"F0.imprint","IMPRINT",EDGE,{"derivedFrom":sQuery(id+"F0.wireOp",EDGE,"E59.bottom")}),1.0]])]});
            extrude(context, id + "F34", {"entities" : qUnion([Q0]), "depth" : 38.1 * mm});
        }
        {
            var Q0;
            Q0=makeQuery(id+"F0.imprint","IMPRINT",FACE,{"disambiguationData":[TD([[makeQuery(id+"F0.imprint","IMPRINT",EDGE,{"derivedFrom":sQuery(id+"F0.wireOp",EDGE,"E60.bottom")}),1.0]])]});
            extrude(context, id + "F35", {"entities" : qUnion([Q0]), "depth" : 38.1 * mm});
        }
        {
            var Q0;
            Q0=makeQuery(id+"F34.opExtrude","CAP_EDGE",EDGE,{"disambiguationData":[OSD([sQuery(id+"F0.wireOp",EDGE,"E59.bottom")])],"isStart":false});
            var Q1;
            Q1=makeQuery(id+"F35.opExtrude","CAP_EDGE",EDGE,{"disambiguationData":[OSD([sQuery(id+"F0.wireOp",EDGE,"E60.bottom")])],"isStart":false});
            var Q2;
            Q2=makeQuery(id+"F34.opExtrude","CAP_EDGE",EDGE,{"disambiguationData":[OSD([sQuery(id+"F0.wireOp",EDGE,"E59.top")])],"isStart":false});
            var Q3;
            Q3=makeQuery(id+"F35.opExtrude","CAP_EDGE",EDGE,{"disambiguationData":[OSD([sQuery(id+"F0.wireOp",EDGE,"E60.top")])],"isStart":false});
            var Q4;
            Q4=makeQuery(id+"F34.opExtrude","CAP_EDGE",EDGE,{"disambiguationData":[OSD([sQuery(id+"F0.wireOp",EDGE,"E59.bottom")])],"isStart":true});
            var Q5;
            Q5=makeQuery(id+"F34.opExtrude","CAP_EDGE",EDGE,{"disambiguationData":[OSD([sQuery(id+"F0.wireOp",EDGE,"E59.top")])],"isStart":true});
            var Q6;
            Q6=makeQuery(id+"F35.opExtrude","CAP_EDGE",EDGE,{"disambiguationData":[OSD([sQuery(id+"F0.wireOp",EDGE,"E60.bottom")])],"isStart":true});
            var Q7;
            Q7=makeQuery(id+"F35.opExtrude","CAP_EDGE",EDGE,{"disambiguationData":[OSD([sQuery(id+"F0.wireOp",EDGE,"E60.top")])],"isStart":true});
            fillet(context, id + "F36", {"entities" : qUnion([Q0, Q1, Q2, Q3, Q4, Q5, Q6, Q7]), "radius" : 5.08 * mm, "tangentPropagation" : true, "allowEdgeOverflow" : false});
        }
        {
            var Q0;
            Q0=makeQuery(id+"F0.imprint","IMPRINT",FACE,{"disambiguationData":[TD([[makeQuery(id+"F0.imprint","IMPRINT",EDGE,{"derivedFrom":sQuery(id+"F0.wireOp",EDGE,"E61.bottom")}),-1.0]])]});
            extrude(context, id + "F37", {"entities" : qUnion([Q0]), "depth" : 38.1 * mm});
        }
        {
            var Q0;
            Q0=makeQuery(id+"F37.opExtrude","CAP_EDGE",EDGE,{"disambiguationData":[OSD([sQuery(id+"F0.wireOp",EDGE,"E61.top")])],"isStart":false});
            var Q1;
            Q1=makeQuery(id+"F37.opExtrude","CAP_EDGE",EDGE,{"disambiguationData":[OSD([sQuery(id+"F0.wireOp",EDGE,"E61.top")])],"isStart":true});
            var Q2;
            Q2=makeQuery(id+"F37.opExtrude","CAP_EDGE",EDGE,{"disambiguationData":[OSD([sQuery(id+"F0.wireOp",EDGE,"E61.bottom")])],"isStart":true});
            var Q3;
            Q3=makeQuery(id+"F37.opExtrude","CAP_EDGE",EDGE,{"disambiguationData":[OSD([sQuery(id+"F0.wireOp",EDGE,"E61.bottom")])],"isStart":false});
            fillet(context, id + "F38", {"entities" : qUnion([Q0, Q1, Q2, Q3]), "radius" : 5.08 * mm, "tangentPropagation" : true, "allowEdgeOverflow" : false});
        }
        {
            var Q0;
            Q0=makeQuery(id+"F0.imprint","IMPRINT",FACE,{"disambiguationData":[TD([[makeQuery(id+"F0.imprint","IMPRINT",EDGE,{"derivedFrom":sQuery(id+"F0.wireOp",EDGE,"E62.bottom")}),-1.0]])]});
            extrude(context, id + "F39", {"entities" : qUnion([Q0]), "depth" : 38.1 * mm});
        }
        {
            var Q0;
            Q0=makeQuery(id+"F39.opExtrude","CAP_EDGE",EDGE,{"disambiguationData":[OSD([sQuery(id+"F0.wireOp",EDGE,"E62.bottom")])],"isStart":false});
            var Q1;
            Q1=makeQuery(id+"F39.opExtrude","CAP_EDGE",EDGE,{"disambiguationData":[OSD([sQuery(id+"F0.wireOp",EDGE,"E62.top")])],"isStart":false});
            var Q2;
            Q2=makeQuery(id+"F39.opExtrude","CAP_EDGE",EDGE,{"disambiguationData":[OSD([sQuery(id+"F0.wireOp",EDGE,"E62.top")])],"isStart":true});
            var Q3;
            Q3=makeQuery(id+"F39.opExtrude","CAP_EDGE",EDGE,{"disambiguationData":[OSD([sQuery(id+"F0.wireOp",EDGE,"E62.bottom")])],"isStart":true});
            fillet(context, id + "F40", {"entities" : qUnion([Q0, Q1, Q2, Q3]), "radius" : 5.08 * mm, "tangentPropagation" : true, "allowEdgeOverflow" : false});
        }
        {
            var Q0;
            Q0=makeQuery(id+"F0.imprint","IMPRINT",FACE,{"disambiguationData":[TD([[makeQuery(id+"F0.imprint","IMPRINT",EDGE,{"derivedFrom":sQuery(id+"F0.wireOp",EDGE,"E63.bottom")}),-1.0]])]});
            extrude(context, id + "F41", {"entities" : qUnion([Q0]), "depth" : 6.35 * mm});
        }
        {
            var Q0;
            Q0=makeQuery(id+"F0.imprint","IMPRINT",FACE,{"disambiguationData":[TD([[makeQuery(id+"F0.imprint","IMPRINT",EDGE,{"derivedFrom":sQuery(id+"F0.wireOp",EDGE,"E64.bottom")}),-1.0]])]});
            extrude(context, id + "F42", {"entities" : qUnion([Q0]), "depth" : 1143 * mm});
        }
        {
            var Q0;
            Q0=makeQuery(id+"F0.imprint","IMPRINT",FACE,{"disambiguationData":[TD([[makeQuery(id+"F0.imprint","IMPRINT",EDGE,{"derivedFrom":sQuery(id+"F0.wireOp",EDGE,"E65.bottom")}),-1.0]])]});
            extrude(context, id + "F43", {"entities" : qUnion([Q0]), "depth" : 1066.8 * mm});
        }
        {
            var Q0;
            Q0=makeQuery(id+"F0.imprint","IMPRINT",FACE,{"disambiguationData":[TD([[makeQuery(id+"F0.imprint","IMPRINT",EDGE,{"derivedFrom":sQuery(id+"F0.wireOp",EDGE,"E66.bottom")}),-1.0]])]});
            extrude(context, id + "F44", {"entities" : qUnion([Q0]), "depth" : 177.8 * mm});
        }
        {
            var Q0;
            Q0=makeQuery(id+"F0.imprint","IMPRINT",FACE,{"disambiguationData":[TD([[makeQuery(id+"F0.imprint","IMPRINT",EDGE,{"derivedFrom":sQuery(id+"F0.wireOp",EDGE,"E67.bottom")}),-1.0]])]});
            extrude(context, id + "F45", {"entities" : qUnion([Q0]), "depth" : 190.5 * mm});
        }
        {
            var Q0;
            Q0=makeQuery(id+"F0.imprint","IMPRINT",FACE,{"disambiguationData":[TD([[makeQuery(id+"F0.imprint","IMPRINT",EDGE,{"derivedFrom":sQuery(id+"F0.wireOp",EDGE,"E68.bottom")}),-1.0]])]});
            extrude(context, id + "F46", {"entities" : qUnion([Q0]), "depth" : 1524 * mm});
        }
        {
            var Q0;
            Q0=makeQuery(id+"F46.opExtrude","SWEPT_FACE",FACE,{"disambiguationData":[OSD([sQuery(id+"F0.wireOp",EDGE,"E68.top")])]});
            var sketch = newSketch(context, id + "F47", { "sketchPlane" : qUnion([Q0])});
            skLineSegment(sketch, "E73.bottom", {"start": v(826.57, 0) * mm, "end": v(731.32, 0) * mm});
            skLineSegment(sketch, "E73.top", {"start": v(826.57, 95.25) * mm, "end": v(731.32, 95.25) * mm});
            skLineSegment(sketch, "E73.left", {"start": v(826.57, 0) * mm, "end": v(826.57, 95.25) * mm});
            skLineSegment(sketch, "E73.right", {"start": v(731.32, 0) * mm, "end": v(731.32, 95.25) * mm});
            skCircle(sketch, "E74", {"center": v(731.32, 95.25) * mm, "radius": 3.18 * mm});
            skLineSegment(sketch, "E75", {"start": v(826.57, 762) * mm, "end": v(731.32, 762) * mm});
            skPoint(sketch, "E75.endSnap0", {"position": v(826.57, 762) * mm});
            skCircle(sketch, "E76", {"center": v(731.32, 762) * mm, "radius": 3.18 * mm});
            skLineSegment(sketch, "E77.bottom", {"start": v(826.57, 1524) * mm, "end": v(731.32, 1524) * mm});
            skLineSegment(sketch, "E77.top", {"start": v(826.57, 1428.75) * mm, "end": v(731.32, 1428.75) * mm});
            skLineSegment(sketch, "E77.left", {"start": v(826.57, 1524) * mm, "end": v(826.57, 1428.75) * mm});
            skLineSegment(sketch, "E77.right", {"start": v(731.32, 1524) * mm, "end": v(731.32, 1428.75) * mm});
            skCircle(sketch, "E78", {"center": v(731.32, 1428.75) * mm, "radius": 3.18 * mm});
            skSolve(sketch);
        }
        {
            var Q0;
            {var subQ0=sQuery(id+"F47.wireOp",EDGE,"E73.right");var subQ1=sQuery(id+"F47.wireOp",EDGE,"E73.top");var subQ2=makeQuery(id+"F47.imprint","INTERSECT",VERTEX,{"derivedFrom":[subQ1,subQ0]});Q0=makeQuery(id+"F47.imprint","IMPRINT",FACE,{"disambiguationData":[TD([[makeQuery(id+"F47.imprint","IMPRINT",EDGE,{"disambiguationData":[TD([[subQ2,1.0]])],"derivedFrom":subQ1}),-1.0]])]});}
            var Q1;
            {var subQ0=sQuery(id+"F47.wireOp",EDGE,"E73.right");var subQ1=sQuery(id+"F47.wireOp",EDGE,"E73.top");var subQ2=makeQuery(id+"F47.imprint","INTERSECT",VERTEX,{"derivedFrom":[subQ1,subQ0]});Q1=makeQuery(id+"F47.imprint","IMPRINT",FACE,{"disambiguationData":[TD([[makeQuery(id+"F47.imprint","IMPRINT",EDGE,{"disambiguationData":[TD([[subQ2,1.0]])],"derivedFrom":subQ1}),1.0]])]});}
            var Q2;
            Q2=makeQuery(id+"F47.imprint","IMPRINT",FACE,{"disambiguationData":[TD([[makeQuery(id+"F47.imprint","IMPRINT",EDGE,{"derivedFrom":sQuery(id+"F47.wireOp",EDGE,"E76")}),1.0]])]});
            var Q3;
            {var subQ0=sQuery(id+"F47.wireOp",EDGE,"E77.right");var subQ1=sQuery(id+"F47.wireOp",EDGE,"E77.top");var subQ2=makeQuery(id+"F47.imprint","INTERSECT",VERTEX,{"derivedFrom":[subQ1,subQ0]});Q3=makeQuery(id+"F47.imprint","IMPRINT",FACE,{"disambiguationData":[TD([[makeQuery(id+"F47.imprint","IMPRINT",EDGE,{"disambiguationData":[TD([[subQ2,1.0]])],"derivedFrom":subQ1}),1.0]])]});}
            var Q4;
            {var subQ0=sQuery(id+"F47.wireOp",EDGE,"E77.right");var subQ1=sQuery(id+"F47.wireOp",EDGE,"E77.top");var subQ2=makeQuery(id+"F47.imprint","INTERSECT",VERTEX,{"derivedFrom":[subQ1,subQ0]});Q4=makeQuery(id+"F47.imprint","IMPRINT",FACE,{"disambiguationData":[TD([[makeQuery(id+"F47.imprint","IMPRINT",EDGE,{"disambiguationData":[TD([[subQ2,1.0]])],"derivedFrom":subQ1}),-1.0]])]});}
            extrude(context, id + "F48", {"entities" : qUnion([Q0, Q1, Q2, Q3, Q4]), "operationType" : NewBodyOperationType.REMOVE, "oppositeDirection" : true, "depth" : 50.8 * mm});
        }
    });
